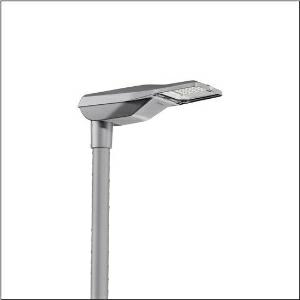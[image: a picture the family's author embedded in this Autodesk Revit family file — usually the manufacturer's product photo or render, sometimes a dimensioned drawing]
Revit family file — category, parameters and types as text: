
# Revit family: streetlight_sl_21_iq_micro___st1_0a_5xe1d41d08cb_ed56
name_source: partatom
category: Lighting Fixtures
units: mm (PartAtom-declared; Revit-internal decimal feet)

## family parameters
Cut with Voids When Loaded = No
Host = Face
Light Source = No
Part Type = Normal
Room Calculation Point = No
Round Connector Dimension = Use Diameter
Shared = No

## types (1)
- --- (1 x LED, 2980 lm, 19.4 W, 4000K)
    Apparent Load = 19 VA
    CIE Flux Codes = 37 72 97 100 100
    Color Rendering = 70
    Color Temperature = 4000K
    Default Elevation = 1800 mm
    Description = Streetlight SL 21 iQ micro, mast luminaire, primary light control with lens, of PMMA, primary optical cover: cover, of toughened safety glass, transparent, light distribution: ST1.0a, light emission: direct distribution, primary light characteristic: asymmetric, installation type: post-top, side-entry, LED, High Power LED, rated luminous flux: 2.980lm, luminous efficacy: 154lm/W, light colour: 740, colour temperature: 4000K, control gear: iQ-Comfort, control: Auto-Match, Temp-Guard, Lumen-Switch, Night-Set, Smart-Wire, Light-Fading, Desk-Remote (wireless, voltage-free reading and setting of iQ features in the workshop via application-optimized NFC function/RFID function), optimised constant luminous flux control (CLO 2.0), pre-setting: linear dimming characteristic, mains connection: 220..240V, AC, 50/60Hz, start of lifetime: 19W, end of service life: 20W, reduction: 10W, luminaire housing, of diecast aluminium, powder-coated, SITECO metallic grey (DB 702S), corrosivity category C5 high according to DIN EN ISO 12944, please order mast flange separately, inclination adjustable: 0°, 5°, 10°, 15°, sealing non-destructively replaceable, multi-level sealing system, length: 528mm, width: 235mm, height: 110mm, mast flange for spigot size: 42mm (side-entry): 5XC10008XM4, 60/48mm (side-entry/post-top): 5XC10108XM2, 76/60mm (side-entry/post-top): 5XC10108XM1, protection rating (complete): IP66, insulation class (complete): insulation class II (safety insulation), certification: CE, ENEC, ENEC+, VDE, impact resistance: IK10, permissible operating ambient temperature for outdoor applications: -40..+50°C, standard-compliant lighting for roads and squares, packaging unit: 1 piece

Light Distribution: ST1.0a
    Height = 110 mm
    Lamp = 1 x LED
    Lamp Light Flux = 2980 lm
    Lamp Power = 19.4 W
    Lamp count = 1
    Length = 528 mm
    Luminous efficacy = 154 lm/W
    Manufacturer = Siteco
    ModVariant = No
    Model = 5XE1D41D08CB
    Number of Poles = 1
    OnlyDefault = Yes
    Power Factor = 1
    Product Name = Streetlight SL 21 iQ micro | ST1.0a
    Product group = mast luminaire | pylon top
    ProductGroupID = 6100
    Protection Class = Protection class II
    Protection Degree = IP 66
    RLX_Detail_Level = 1
    RLX_Emergency_Light_Flux = 0 lm
    RLX_Emergency_Type = 0
    RLX_Emergency_Type_DB = No
    RlxData = <blob elided: 98493 chars, md5=152d231c>
    Socket = socket
    Standby Power = 0 W
    System Light Flux = 2980 lm
    System Power = 19 W
    Type Comments = factory setting: luminous flux: 100 % | dim-lin: 254 | 387 mA
    Type Image = l_1006881.jpg
    URL = http://relux.com
    VarID = @adj_138711
    Voltage = 0 V
    Weight = 0.00 kg
    Width = 235 mm

## geometry (parser evidence)
native form markers: Blend x4, Sweep x11
no freeform markers — native parametric forms only
